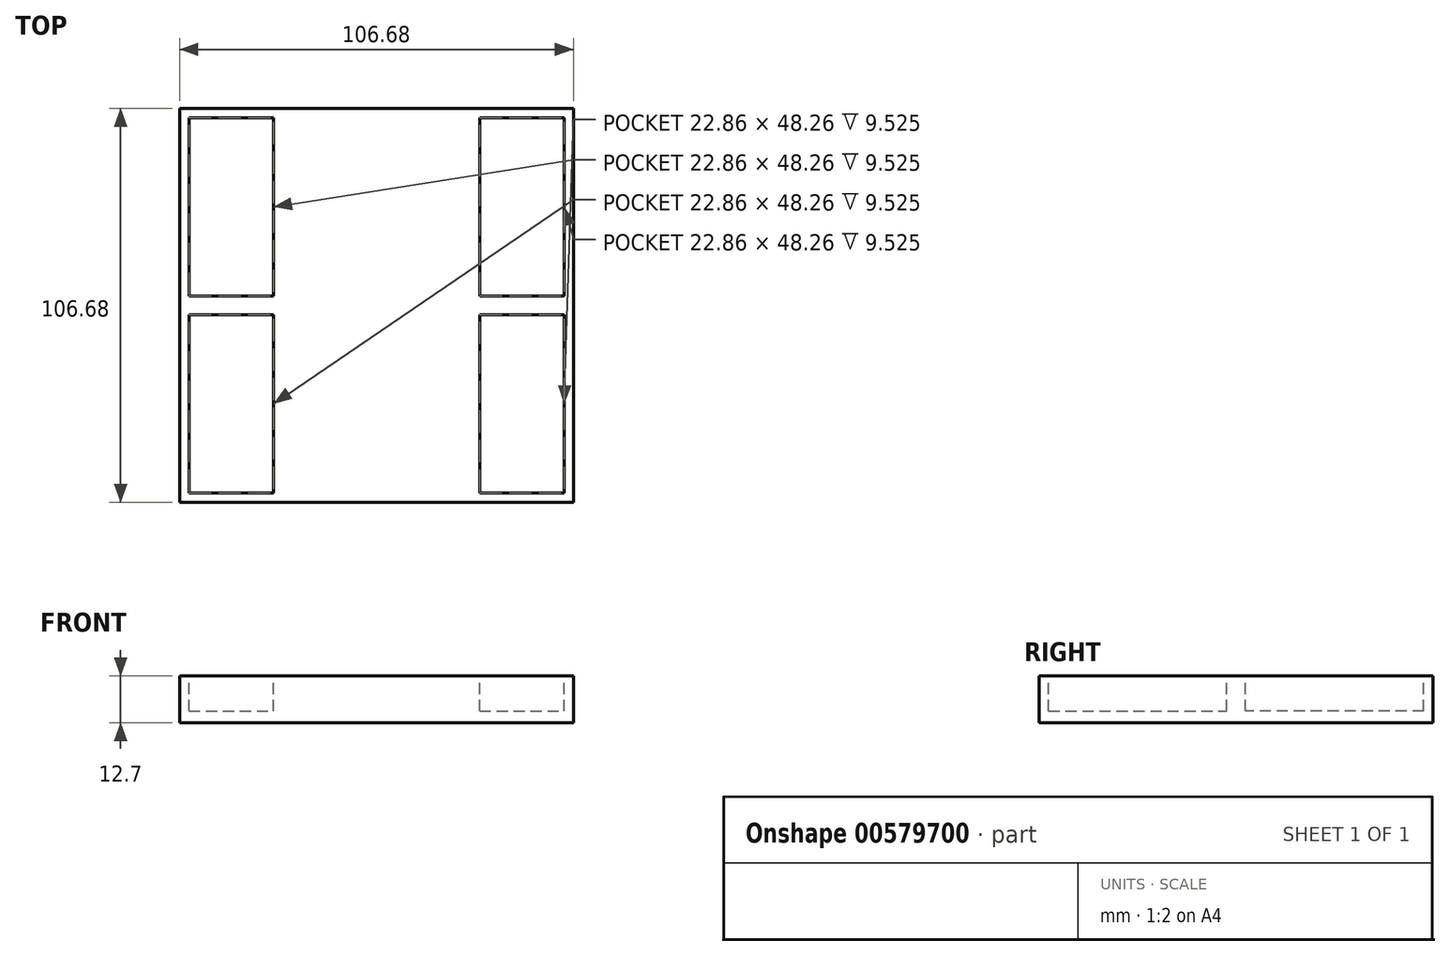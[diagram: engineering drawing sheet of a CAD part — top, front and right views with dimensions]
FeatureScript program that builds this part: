
annotation { "Feature Type Name" : "Feature", "Feature Type Description" : "" }
export const myFeature = defineFeature(function(context is Context, id is Id, definition is map)
    precondition{}
    {
        {
            var Q0;
            Q0=qCreatedBy(makeId("Top.planeOp"),FACE);
            var sketch = newSketch(context, id + "F0", { "sketchPlane" : qUnion([Q0])});
            skLineSegment(sketch, "E0.bottom", {"start": v(53.34, 53.34) * mm, "end": v(-53.34, 53.34) * mm});
            skLineSegment(sketch, "E0.top", {"start": v(53.34, -53.34) * mm, "end": v(-53.34, -53.34) * mm});
            skLineSegment(sketch, "E0.left", {"start": v(53.34, 53.34) * mm, "end": v(53.34, -53.34) * mm});
            skLineSegment(sketch, "E0.right", {"start": v(-53.34, 53.34) * mm, "end": v(-53.34, -53.34) * mm});
            skPoint(sketch, "E0.middle", {"position": v(0, 0) * mm});
            skSolve(sketch);
        }
        {
            var Q0;
            Q0=makeQuery(id+"F0.imprint","IMPRINT",FACE,{"disambiguationData":[TD([[makeQuery(id+"F0.imprint","IMPRINT",EDGE,{"derivedFrom":sQuery(id+"F0.wireOp",EDGE,"E0.bottom")}),1.0]])]});
            extrude(context, id + "F1", {"entities" : qUnion([Q0]), "depth" : 12.7 * mm, "offsetDistance" : 25.4 * mm});
        }
        {
            var Q0;
            Q0=makeQuery(id+"F1.opExtrude","CAP_FACE",FACE,{"disambiguationData":[OSD([sQuery(id+"F0.wireOp",EDGE,"E0.bottom"),sQuery(id+"F0.wireOp",EDGE,"E0.top"),sQuery(id+"F0.wireOp",EDGE,"E0.left"),sQuery(id+"F0.wireOp",EDGE,"E0.right")])],"isStart":false});
            var sketch = newSketch(context, id + "F2", { "sketchPlane" : qUnion([Q0])});
            skLineSegment(sketch, "E1.bottom", {"start": v(-50.8, -50.8) * mm, "end": v(-27.94, -50.8) * mm});
            skLineSegment(sketch, "E1.top", {"start": v(-50.8, -2.54) * mm, "end": v(-27.94, -2.54) * mm});
            skLineSegment(sketch, "E1.left", {"start": v(-50.8, -50.8) * mm, "end": v(-50.8, -2.54) * mm});
            skLineSegment(sketch, "E1.right", {"start": v(-27.94, -50.8) * mm, "end": v(-27.94, -2.54) * mm});
            skLineSegment(sketch, "E2.bottom", {"start": v(-50.8, 50.8) * mm, "end": v(-27.94, 50.8) * mm});
            skLineSegment(sketch, "E2.top", {"start": v(-50.8, 2.54) * mm, "end": v(-27.94, 2.54) * mm});
            skLineSegment(sketch, "E2.left", {"start": v(-50.8, 50.8) * mm, "end": v(-50.8, 2.54) * mm});
            skLineSegment(sketch, "E2.right", {"start": v(-27.94, 50.8) * mm, "end": v(-27.94, 2.54) * mm});
            skLineSegment(sketch, "E3.bottom", {"start": v(50.8, 50.8) * mm, "end": v(27.94, 50.8) * mm});
            skLineSegment(sketch, "E3.top", {"start": v(50.8, 2.54) * mm, "end": v(27.94, 2.54) * mm});
            skLineSegment(sketch, "E3.left", {"start": v(50.8, 50.8) * mm, "end": v(50.8, 2.54) * mm});
            skLineSegment(sketch, "E3.right", {"start": v(27.94, 50.8) * mm, "end": v(27.94, 2.54) * mm});
            skLineSegment(sketch, "E4.bottom", {"start": v(27.94, -50.8) * mm, "end": v(50.8, -50.8) * mm});
            skLineSegment(sketch, "E4.top", {"start": v(27.94, -2.54) * mm, "end": v(50.8, -2.54) * mm});
            skLineSegment(sketch, "E4.left", {"start": v(27.94, -50.8) * mm, "end": v(27.94, -2.54) * mm});
            skLineSegment(sketch, "E4.right", {"start": v(50.8, -50.8) * mm, "end": v(50.8, -2.54) * mm});
            skSolve(sketch);
        }
        {
            var Q0;
            Q0=makeQuery(id+"F2.imprint","IMPRINT",FACE,{"disambiguationData":[TD([[makeQuery(id+"F2.imprint","IMPRINT",EDGE,{"derivedFrom":sQuery(id+"F2.wireOp",EDGE,"E4.bottom")}),1.0]])]});
            var Q1;
            Q1=makeQuery(id+"F2.imprint","IMPRINT",FACE,{"disambiguationData":[TD([[makeQuery(id+"F2.imprint","IMPRINT",EDGE,{"derivedFrom":sQuery(id+"F2.wireOp",EDGE,"E3.bottom")}),1.0]])]});
            var Q2;
            Q2=makeQuery(id+"F2.imprint","IMPRINT",FACE,{"disambiguationData":[TD([[makeQuery(id+"F2.imprint","IMPRINT",EDGE,{"derivedFrom":sQuery(id+"F2.wireOp",EDGE,"E1.bottom")}),1.0]])]});
            var Q3;
            Q3=makeQuery(id+"F2.imprint","IMPRINT",FACE,{"disambiguationData":[TD([[makeQuery(id+"F2.imprint","IMPRINT",EDGE,{"derivedFrom":sQuery(id+"F2.wireOp",EDGE,"E2.bottom")}),-1.0]])]});
            extrude(context, id + "F3", {"entities" : qUnion([Q0, Q1, Q2, Q3]), "operationType" : NewBodyOperationType.REMOVE, "oppositeDirection" : true, "depth" : 9.52 * mm, "offsetDistance" : 25.4 * mm});
        }
    });
